# Revit family: Boiler-WM-SVF-1500-2000
name_source: partatom
category: Mechanical Equipment
units: mm (PartAtom-declared; Revit-internal decimal feet)

## family parameters
Always vertical = Yes
Cut with Voids When Loaded = No
OmniClass Number = 23.75.10.11.14
OmniClass Title = Hot Water Heat Generators
Part Type = Normal
Room Calculation Point = No
Round Connector Dimension = Use Diameter
Shared = No
Work Plane-Based = Yes

## types (1)
- boiler
    Boiler Return Water Diameter = 0"
    Boiler Supply Water Diameter = 0"
    Condensate Drain Connection Diameter = 0"
    Dead Weight = 0
    Default Elevation = 0 "
    Flue Diameter = 0"
    Frame Accent Material = Plastic - WeilMcLain - Black
    Frame Finish = Metal - WeilMcLain - Gray
    Frequency = 60 Hz
    Full Load Current = 0 A
    Gas Connection Diameter = 0"
    Height = 0 "
    Length = 0 "
    Net AHRI MBH = 0.0 Btu/h
    Number of Poles = 1
    Operating Temperature = 0
    Operating Weight = 0
    Phase = 1
    Screen Material = Plastic - WeilMcLain - Blue
    Standards Conformance = ASME  ;  AHRI  ;  CSA
    Supply Air Connection Diameter = 0"
    Tank Capacity = 0 gal
    Thermal Efficiency = 0
    Total Heating Capacity = 0.0 Btu/h
    Voltage = 0 V
    Width = 0 "

## geometry (parser evidence)
native form markers: Sweep x2
no freeform markers — native parametric forms only
